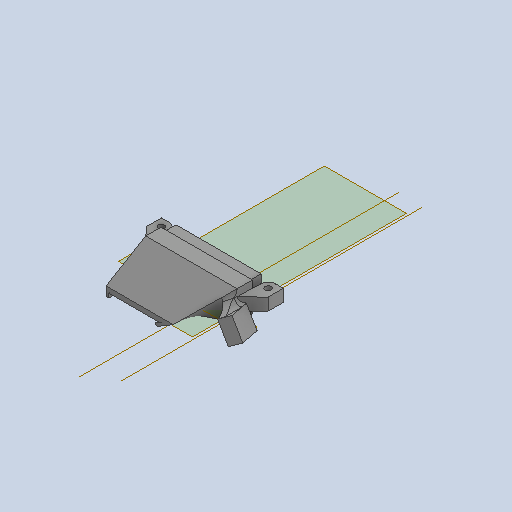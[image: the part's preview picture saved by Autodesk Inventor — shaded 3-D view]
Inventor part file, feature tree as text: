
AUTODESK INVENTOR PART (.ipt)
format: ipt  version: 2022 (Build 260153000, 153)  size: 507,392 bytes
history: native  units: mm
features: other x14, extrude x10, sketch x10, reference x7, plane x4, projected_geometry x4, fillet x3, loft x2, chamfer x2, shell x1, pattern_circular x1
ambient origin geometry x8: Origin, YZ Plane, XZ Plane, XY Plane, X Axis, Y Axis, Z Axis, Center Point
bodies: Solid1 (feature_tree)
feature tree (58):
  extrude  "Extrusion1"  Depth=1.0mm
  extrude  "Extrusion2"  Depth=5.0mm TaperAngle=0.0deg
  plane  "Work Plane1"
  sketch  "Sketch3"  dims[d6=3.0mm d7=15.0mm]
  extrude  "Extrusion3"  Depth=15.0mm
  extrude  "Extrusion4"  TaperAngle=0.0deg  [1 undecoded]
  loft  "Loft1"
  loft  "Loft2"
  shell  "Shell3"  Thickness=0.0mm
  plane  "Work Plane2"
  extrude  "Extrusion5"  Depth=0.01mm TaperAngle=0.0deg
  plane  "Work Plane4"
  extrude  "Extrusion6"  TaperAngle=0.0deg  [1 undecoded]
  other  "Work Axis1"
  pattern_circular  "Circular Pattern1"  Angle=90.0deg  [1 undecoded]
  chamfer  "Chamfer1"  Distance=0.88mm
  chamfer  "Chamfer2"  [1 undecoded]
  other  "Work Axis2"
  fillet  "Fillet3"  Radius=5.0mm
  extrude  "Extrusion7"  Depth=4.0mm
  plane  "Work Plane5"
  extrude  "Extrusion8"  TaperAngle=0.0deg  [1 undecoded]
  extrude  "Extrusion9"  Depth=8.0mm
  fillet  "Fillet5"  Radius=4.0mm
  fillet  "Fillet6"  [1 undecoded]
  extrude  "Extrusion10"  Depth=3.0mm
  sketch  "Sketch1"  dims[d0=0.15mm d1=1.0mm]
  reference  "Reference1"
  reference  "Reference2"
  sketch  "Sketch2"  dims[d2=4.0mm d3=0.0mm d4=5.0mm d5=0.0mm]
  reference  "Reference3"
  projected_geometry  "Projected Loop1"
  reference  "Reference4"
  sketch  "Sketch4"  dims[d8=3.0mm d9=0.0mm]
  other  "Edges1"
  other  "Edges3"
  other  "Edges4"
  other  "Edges5"
  sketch  "Sketch5"  dims[d10=1.0mm d11=1.0mm]
  sketch  "Sketch7"  dims[d12=20.0mm d13=4.0mm d14=0.0mm]
  sketch  "Sketch8"  dims[d15=1.0mm d17=0.01mm d18=0.0mm]
  sketch  "Sketch9"  dims[d19=0.5mm d20=0.0mm d21=0.0mm d22=90.0deg]
  sketch  "Sketch10"  dims[d25=0.0mm d26=90.0deg]
  reference  "Reference7"
  reference  "Reference8"
  reference  "Reference9"
  projected_geometry  "Projected Loop2"
  sketch  "Sketch11"  dims[d28=0.0mm d29=90.0deg d30=0.0mm d31=90.0deg d34=0.88mm d35=-3.4mm d36=5.0mm d37=0.0mm d45=4.0mm d47=0.0mm d50=8.0mm d51=4.0mm d52=90.0deg d54=3.0mm d55=7.0mm d56=0.0mm d57=30.0mm d58=30.0deg d60=3.5mm d61=2.0mm d62=45.0deg d63=2.5mm d64=2.0mm d65=45.0deg d66=15.0mm d67=1.6mm d69=7.0mm d70=0.0mm d71=-15.0mm d72=2.0mm d73=0.0mm d74=3.0mm d75=0.5mm d76=0.0mm d77=1.6mm d78=5.8mm d79=1.0mm d80=0.0mm d27=0.0mm]
  projected_geometry  "Projected Loop3"
  projected_geometry  "Projected Loop4"
  other  "Volcano_Printhead.iam"
  other  "4010 turbo fan v3:1"
  other  "4010 turbo fan v3:3"
  other  "E3D-VOLCANO-1.75-MO:2"
  other  "Assembly1"
  other  "volcano tool.iam"
  other  "Toolplate  V2:1"
  other  "E3D-VOLCANO-1.75-MO:1"
note: 6 required parameter values undecoded (feature->parameter linkage not recoverable at this tier; creation-order binding heuristic only, values carry confidence <= 0.55)
